# Revit family: Normann_ENTRY_ETR2_3A-R290
name_source: partatom
category: Attrezzature speciali
units: mm (PartAtom-declared; Revit-internal decimal feet)

## family parameters
Basato su piano di lavoro = No
Condiviso = No
Punto di calcolo locali = No
Quota connettore circolare = Usa diametro
Sempre verticale = Sì
Taglio con vuoti quando caricato = No
Tipo di parte = Normale

## types (2) — shared parameters
Asset Identifier = ETR2/3A-R290
Capacity internal - L = 31
Condensation = AIR
Controller = EVJ805
Depth Actual = 592 mm  [stored 1.94226 ft]
Depth Body = 592 mm  [stored 1.94226 ft]
Door Side R_L = No
Door_DX = No
Door_SX = Sì
Feet = Sì
GWP = 3
Gross Weight kg = 139
H_Feet_Limits = 125 mm  [stored 0.410105 ft]
Height Actual = 636 mm  [stored 2.08661 ft]
Height_Door = 338 mm  [stored 1.10892 ft]
Height_Feet_100to160 = 125 mm  [stored 0.410105 ft]
Height_Feet_Actual = 125 mm  [stored 0.410105 ft]
Internal depth actual - mm = 364 mm  [stored 1.19423 ft]
Internal height actual - mm = 250 mm  [stored 0.82021 ft]
Internal length actual - mm = 340 mm  [stored 1.11549 ft]
Length Actual = 440 mm  [stored 1.44357 ft]
Manufacturer = Normann
Mat_Frame = Acciaio inox, spazzolato
Mat_Grid = Acciaio inox, spazzolato
Max current cold cycle - A = 1.63
Max power cold cycle - W = 327
Model Category = Blast chiller reach-in
Model Series = Entry
Net Weight kg = 124
OffSet_Display = 68 mm
Optional = CORE PROBE
Packaging depth actual - mm = 610 mm  [stored 2.00131 ft]
Packaging height actual - mm = 690 mm  [stored 2.26378 ft]
Packaging length actual - mm = 460 mm  [stored 1.50919 ft]
Packing volume - m3 = 0.2
Power Supply (Volts/Ph/Hz) = 220-240/1N/50
Refrigerant gas = R290
Refrigeration Climate Class = 4
Temperature range - °C = -40/+3
Tray Type = GN2/3 (325 x 354 mm)
Tray number = 3
URL Manufacturer = https://www.normann.it
Wheel = No
Wheel_Feet = No
Yield per blast chiling cycle (+90°C/+3°C) - kg = 6
Yield per blast chiling cycle +65/+10°C (EN22042) - kg = 4
Yield per blast chiling cycle energy consumed (EN22042) - kWh/kg = 0.087
Yield per blast chiling cycle test time (EN22042) - min = 97
Yield per shock freezing cycle (+90/-18°C) - kg = 4
Yield per shock freezing cycle +65/-18°C (EN22042) - kg = 2
Yield per shock freezing cycle energy consumed (EN22042) - kWh/kg = 0.223
Yield per shock freezing cycle test time (EN22042) - min = 270
zero-valued in all types: Ice cream pan 5l quantity (360x165x120mm), Liquid line diameter - mm, Max current warm cycle - A, Max power warm cycle - W, Prospetto di default, Suction line diameter - mm, Tray quantity EN1-GN1/1 h20mm, Tray quantity EN1-GN1/1 h40mm, Tray quantity EN1-GN1/1 h65mm, Tray quantity GN2/3 h65mm, Yield per blast chiling cycle consumption (EN22042) - kWh, Yield per shock freezing cycle consuption (EN22042) - kWh

## per-type parameters (varying)
| type | ID |
| ENTRY2/3 AIR, R290, 220-240/1N/50, EVJ805, LHH, FEET | 5A1D1A3B1-03A1E |
| ENTRY2/3 AIR, R290, 220-240/1N/50, EVJ805, RHH, FEET | 5A1D1A3B1-03A2E |

note: [stored X ft] marks values corroborated as IEEE doubles in the binary element streams (Revit-internal decimal feet)
